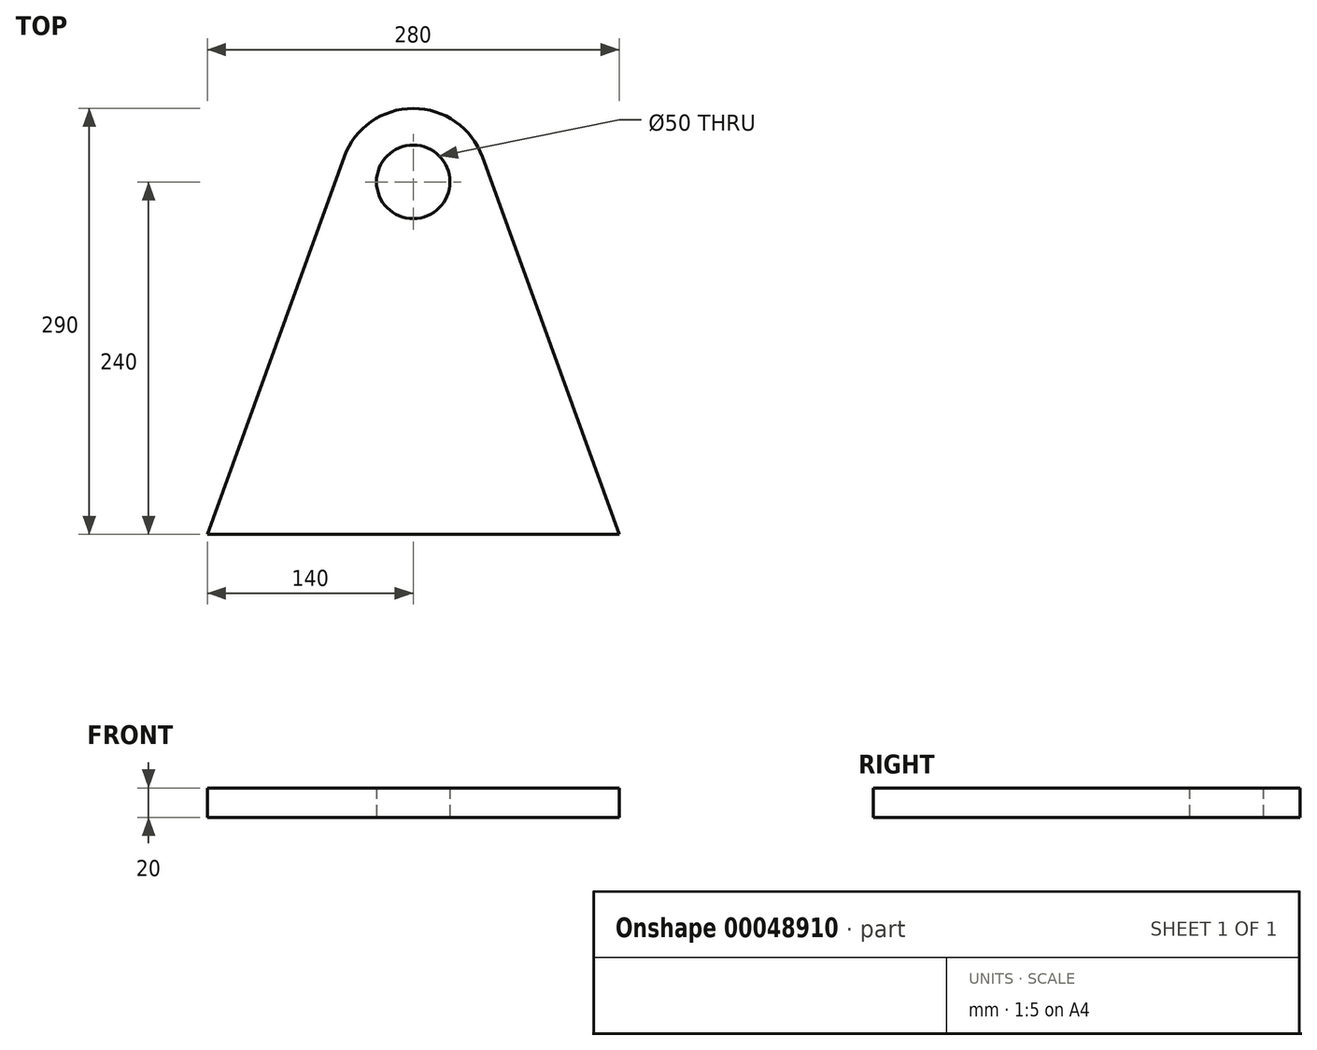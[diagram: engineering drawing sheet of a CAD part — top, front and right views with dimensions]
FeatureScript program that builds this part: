
annotation { "Feature Type Name" : "Feature", "Feature Type Description" : "" }
export const myFeature = defineFeature(function(context is Context, id is Id, definition is map)
    precondition{}
    {
        {
            var Q0;
            Q0=qCreatedBy(makeId("Top.planeOp"),FACE);
            var sketch = newSketch(context, id + "F0", { "sketchPlane" : qUnion([Q0])});
            skCircle(sketch, "E0", {"center": v(0, 0) * mm, "radius": 50 * mm});
            skCircle(sketch, "E1", {"center": v(0, 0) * mm, "radius": 25 * mm});
            skLineSegment(sketch, "E2", {"start": v(0, 0) * mm, "end": v(0, -240) * mm, "construction": true});
            skLineSegment(sketch, "E3", {"start": v(0, -240) * mm, "end": v(140, -240) * mm});
            skLineSegment(sketch, "E4", {"start": v(0, -240) * mm, "end": v(-140, -240) * mm});
            skLineSegment(sketch, "E5", {"start": v(-140, -240) * mm, "end": v(-47.02, 17.01) * mm});
            skLineSegment(sketch, "E6", {"start": v(140, -240) * mm, "end": v(47.02, 17.01) * mm});
            skSolve(sketch);
        }
        {
            var Q0;
            Q0 = qSketchRegion(id + "F0", true);
            extrude(context, id + "F1", {"entities" : qUnion([Q0]), "depth" : 20 * mm});
        }
    });
